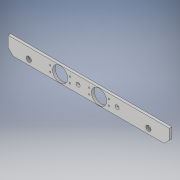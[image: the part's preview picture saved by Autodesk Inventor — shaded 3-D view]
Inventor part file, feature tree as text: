
AUTODESK INVENTOR PART (.ipt)
format: ipt  version: 2017 (Build 210142000, 142)  size: 147,968 bytes
history: native  units: in
note: dims shown in document units (in); Inventor stores cm internally (conversion verified against a paired STEP export)
features: extrude x4, chamfer x3, sketch x1, hole x1
ambient origin geometry x8: Origin, YZ Plane, XZ Plane, XY Plane, X Axis, Y Axis, Z Axis, Center Point
bodies: Solid1 (feature_tree)
feature tree (9):
  sketch  "Sketch1"  dims[d0=1.5in d1=15.5in d3=1.46in d5=1.46in d6=0.25in d7=0.0in d10=0.14in d11=0.14in d12=0.14in d13=0.75in d14=0.375in d15=0.25in d16=0.5635in d17=1.0in d18=0.8108in d19=0.125in d20=0.125in d21=45.0deg d24=0.276in d28=0.138in d29=0.138in d30=0.138in d31=0.945in d38=0.138in d39=0.138in d40=0.138in d41=0.138in d42=0.25in d43=0.0in d44=0.25in d45=0.0in d48=0.5in d50=0.5in d51=1.0in d52=0.0in d53=0.5in d54=0.125in d55=45.0deg d56=0.5in d57=0.125in d58=45.0deg]
  extrude  "Extrusion1"  Depth=15.5in
  hole  "Hole1"  [1 undecoded]
  chamfer  "Chamfer1"  Distance=1.46in
  extrude  "Extrusion2"  Depth=0.25in TaperAngle=0.0deg
  extrude  "Extrusion3"  Depth=0.25in
  extrude  "Extrusion4"  Depth=0.25in
  chamfer  "Chamfer2"  Distance=0.125in Angle=45.0deg
  chamfer  "Chamfer3"  Distance=0.276in
note: 1 required parameter value undecoded (feature->parameter linkage not recoverable at this tier; creation-order binding heuristic only, values carry confidence <= 0.55)
